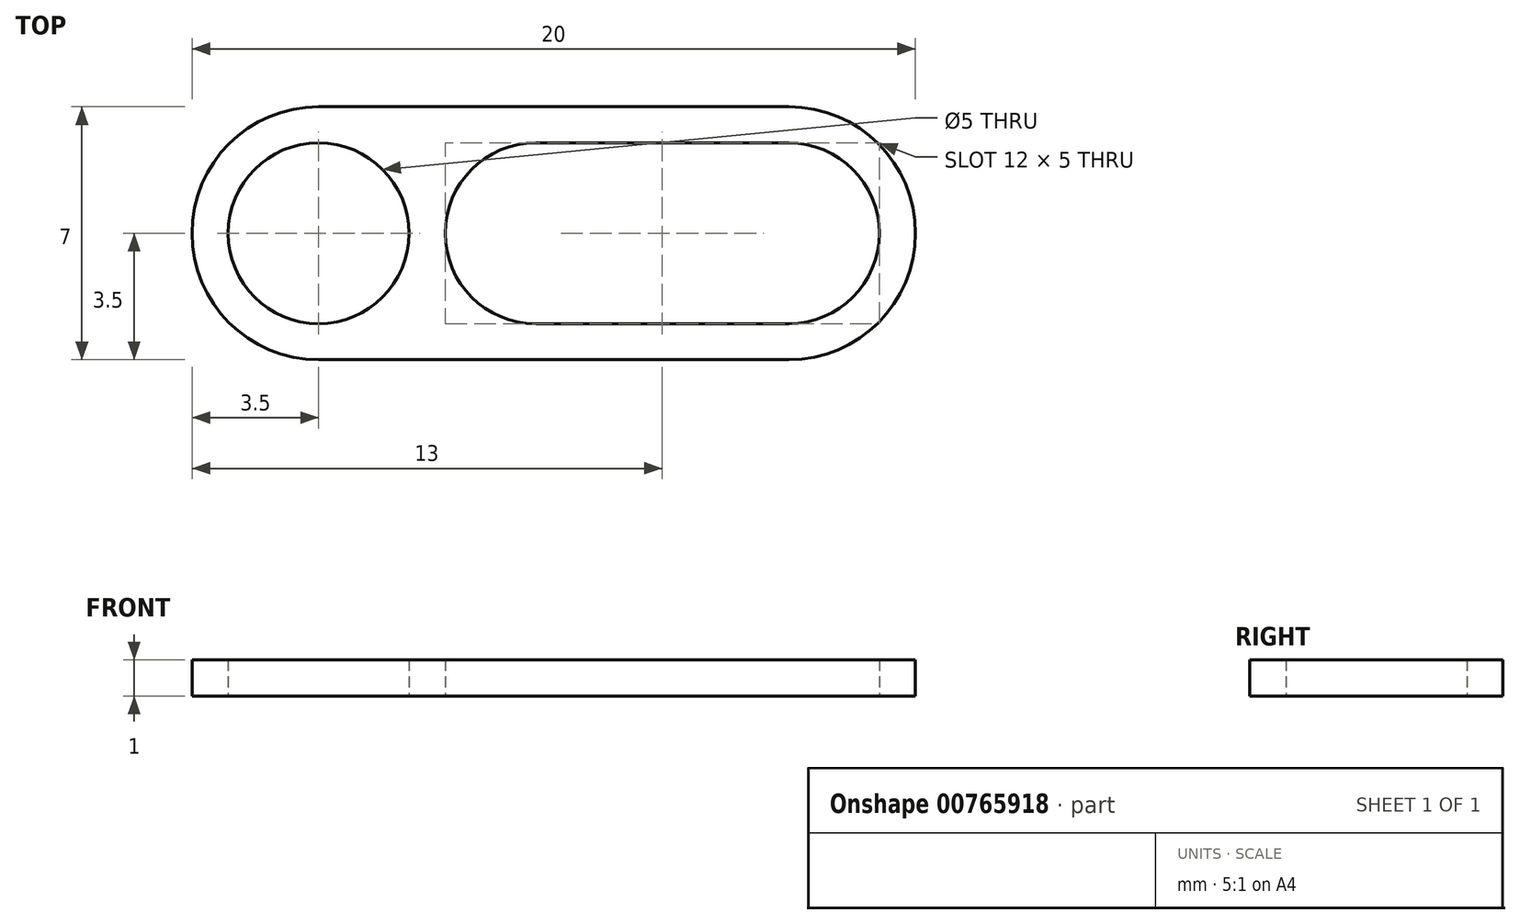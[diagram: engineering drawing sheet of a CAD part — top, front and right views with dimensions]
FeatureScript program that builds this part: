
annotation { "Feature Type Name" : "Feature", "Feature Type Description" : "" }
export const myFeature = defineFeature(function(context is Context, id is Id, definition is map)
    precondition{}
    {
        {
            var Q0;
            Q0=qCreatedBy(makeId("Top.planeOp"),FACE);
            var sketch = newSketch(context, id + "F0", { "sketchPlane" : qUnion([Q0])});
            skCircle(sketch, "E0", {"center": v(0, 0) * mm, "radius": 2.5 * mm});
            skCircle(sketch, "E1", {"center": v(0, 0) * mm, "radius": 3.5 * mm});
            skLineSegment(sketch, "E2", {"start": v(0, 0) * mm, "end": v(13, 0) * mm});
            skLineSegment(sketch, "E3", {"start": v(0, 0) * mm, "end": v(6, 0) * mm});
            skCircle(sketch, "E4", {"center": v(6, 0) * mm, "radius": 2.5 * mm});
            skCircle(sketch, "E5", {"center": v(13, 0) * mm, "radius": 2.5 * mm});
            skCircle(sketch, "E6", {"center": v(13, 0) * mm, "radius": 3.5 * mm});
            skLineSegment(sketch, "E7", {"start": v(6, 2.5) * mm, "end": v(13, 2.5) * mm});
            skLineSegment(sketch, "E8", {"start": v(6, -2.5) * mm, "end": v(13, -2.5) * mm});
            skLineSegment(sketch, "E9", {"start": v(0, -3.5) * mm, "end": v(13, -3.5) * mm});
            skLineSegment(sketch, "E10", {"start": v(0, 3.5) * mm, "end": v(13, 3.5) * mm});
            skSolve(sketch);
        }
        {
            assignVariable(context, id + "F1", {"name" : "height", "anyValue" : 1});
        }
        {
            var Q0;
            {var subQ7=sQuery(id+"F0.wireOp",EDGE,"E9");Q0=makeQuery(id+"F0.imprint","IMPRINT",FACE,{"disambiguationData":[TD([[makeQuery(id+"F0.imprint","IMPRINT",EDGE,{"derivedFrom":subQ7}),1.0]])]});}
            var Q1;
            {var subQ5=sQuery(id+"F0.wireOp",EDGE,"E7");var subQ7=sQuery(id+"F0.wireOp",EDGE,"E5");var subQ8=makeQuery(id+"F0.imprint","INTERSECT",VERTEX,{"derivedFrom":[subQ7,subQ5]});Q1=makeQuery(id+"F0.imprint","IMPRINT",FACE,{"disambiguationData":[TD([[makeQuery(id+"F0.imprint","IMPRINT",EDGE,{"disambiguationData":[TD([[subQ8,1.0]])],"derivedFrom":subQ7}),-1.0]])]});}
            var Q2;
            {var subQ7=sQuery(id+"F0.wireOp",EDGE,"E10");Q2=makeQuery(id+"F0.imprint","IMPRINT",FACE,{"disambiguationData":[TD([[makeQuery(id+"F0.imprint","IMPRINT",EDGE,{"derivedFrom":subQ7}),-1.0]])]});}
            var Q3;
            Q3=makeQuery(id+"F0.imprint","IMPRINT",FACE,{"disambiguationData":[TD([[makeQuery(id+"F0.imprint","IMPRINT",EDGE,{"derivedFrom":sQuery(id+"F0.wireOp",EDGE,"E0")}),-1.0]])]});
            extrude(context, id + "F2", {"entities" : qUnion([Q0, Q1, Q2, Q3]), "depth" : (getVariable(context, 'height')) * mm, "offsetDistance" : 25 * mm});
        }
    });
